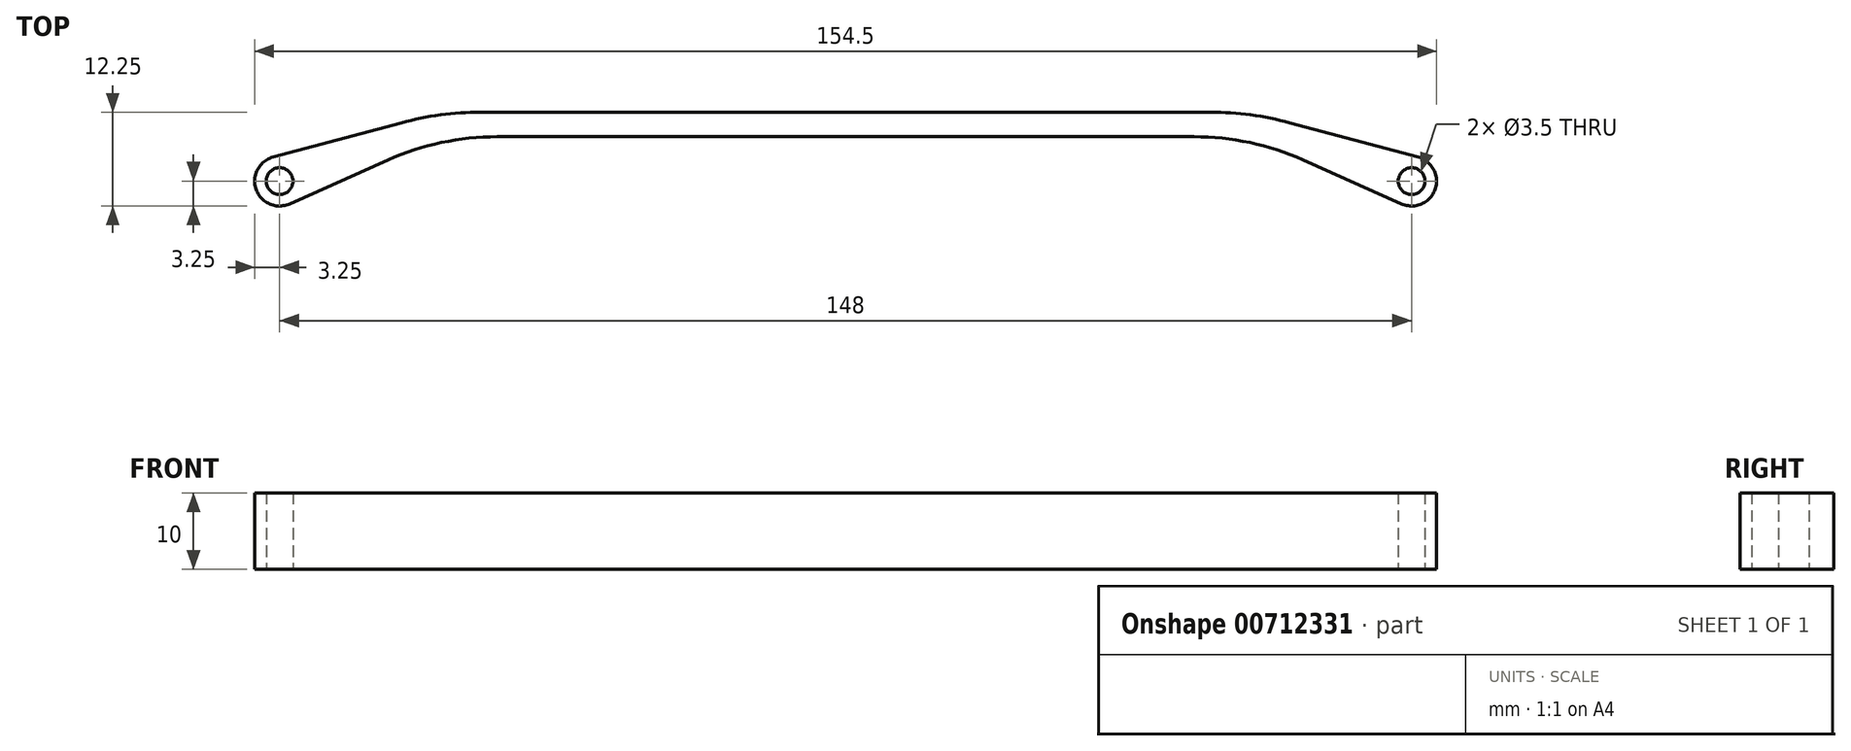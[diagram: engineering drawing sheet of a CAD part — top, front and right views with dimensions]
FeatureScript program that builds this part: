
annotation { "Feature Type Name" : "Feature", "Feature Type Description" : "" }
export const myFeature = defineFeature(function(context is Context, id is Id, definition is map)
    precondition{}
    {
        {
            var Q0;
            Q0=qCreatedBy(makeId("Top.planeOp"),FACE);
            var sketch = newSketch(context, id + "F0", { "sketchPlane" : qUnion([Q0])});
            skLineSegment(sketch, "E0", {"start": v(0, 38.57) * mm, "end": v(0, -46.29) * mm, "construction": true});
            skLineSegment(sketch, "E1", {"start": v(0, 0) * mm, "end": v(53, 0) * mm});
            skLineSegment(sketch, "E2.0", {"start": v(0, -3.2) * mm, "end": v(53, -3.2) * mm});
            skLineSegment(sketch, "E3", {"start": v(0, 0) * mm, "end": v(53, 0) * mm, "construction": true});
            skLineSegment(sketch, "E4", {"start": v(74, 0) * mm, "end": v(74, -9) * mm, "construction": true});
            skCircle(sketch, "E5", {"center": v(74, -9) * mm, "radius": 1.75 * mm});
            skArc(sketch, "E6", {"start": v(72.68, -11.97) * mm, "mid": v(77.18, -9.68) * mm, "end": v(74, -5.75) * mm});
            skLineSegment(sketch, "E7", {"start": v(53, 0) * mm, "end": v(74.84, -5.86) * mm});
            skLineSegment(sketch, "E8", {"start": v(53, -3.2) * mm, "end": v(72.68, -11.97) * mm});
            skLineSegment(sketch, "E9.MirrorCS", {"start": v(-53, -3.2) * mm, "end": v(-72.68, -11.97) * mm});
            skLineSegment(sketch, "E10.MirrorCS", {"start": v(0, -3.2) * mm, "end": v(-53, -3.2) * mm});
            skLineSegment(sketch, "E11.MirrorCS", {"start": v(0, 0) * mm, "end": v(-53, 0) * mm, "construction": true});
            skLineSegment(sketch, "E12.MirrorCS", {"start": v(-53, 0) * mm, "end": v(-74.84, -5.86) * mm});
            skArc(sketch, "E13.MirrorCS", {"start": v(-72.68, -11.97) * mm, "mid": v(-77.18, -9.68) * mm, "end": v(-74, -5.75) * mm});
            skCircle(sketch, "E14.MirrorC", {"center": v(-74, -9) * mm, "radius": 1.75 * mm});
            skLineSegment(sketch, "E15", {"start": v(-53, 0) * mm, "end": v(0, 0) * mm});
            skSolve(sketch);
        }
        {
            var Q0;
            Q0=makeQuery(id+"F0.imprint","IMPRINT",FACE,{"disambiguationData":[TD([[makeQuery(id+"F0.imprint","IMPRINT",EDGE,{"derivedFrom":sQuery(id+"F0.wireOp",EDGE,"E1")}),-1.0]])]});
            extrude(context, id + "F1", {"entities" : qUnion([Q0]), "depth" : 10 * mm, "offsetDistance" : 25 * mm});
        }
        {
            var Q0;
            Q0=makeQuery(id+"F1.opExtrude","SWEPT_EDGE",EDGE,{"disambiguationData":[OSD([sQuery(id+"F0.wireOp",EDGE,"E1"),sQuery(id+"F0.wireOp",EDGE,"E7")])]});
            var Q1;
            Q1=makeQuery(id+"F1.opExtrude","SWEPT_EDGE",EDGE,{"disambiguationData":[OSD([sQuery(id+"F0.wireOp",EDGE,"E12.MirrorCS"),sQuery(id+"F0.wireOp",EDGE,"E15")])]});
            fillet(context, id + "F2", {"entities" : qUnion([Q0, Q1]), "tangentPropagation" : true, "radius" : 40 * mm, "defaultsChanged" : true, "vertexSettings" : [], "allowEdgeOverflow" : false});
        }
        {
            var Q0;
            Q0=makeQuery(id+"F1.opExtrude","SWEPT_EDGE",EDGE,{"disambiguationData":[OSD([sQuery(id+"F0.wireOp",EDGE,"E9.MirrorCS"),sQuery(id+"F0.wireOp",EDGE,"E10.MirrorCS")])]});
            var Q1;
            Q1=makeQuery(id+"F1.opExtrude","SWEPT_EDGE",EDGE,{"disambiguationData":[OSD([sQuery(id+"F0.wireOp",EDGE,"E2.0"),sQuery(id+"F0.wireOp",EDGE,"E8")])]});
            fillet(context, id + "F3", {"entities" : qUnion([Q0, Q1]), "tangentPropagation" : true, "radius" : 35 * mm, "defaultsChanged" : true, "vertexSettings" : [], "allowEdgeOverflow" : false});
        }
    });
